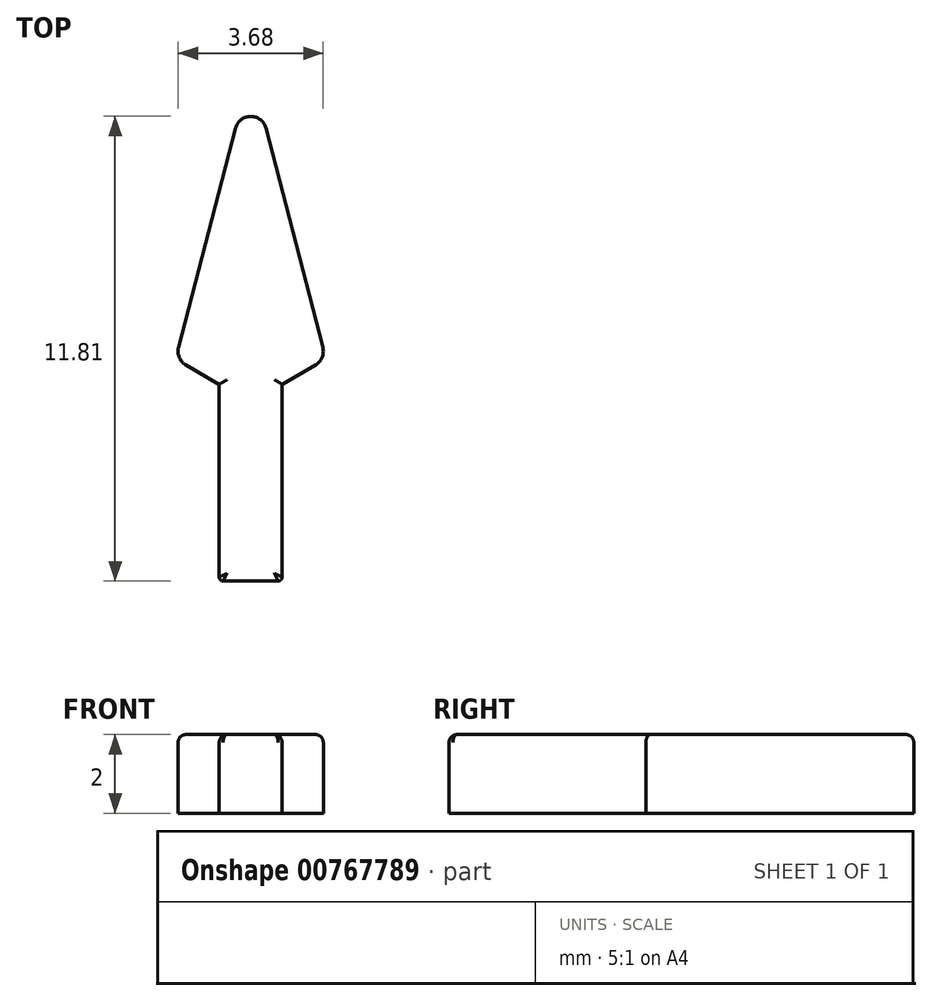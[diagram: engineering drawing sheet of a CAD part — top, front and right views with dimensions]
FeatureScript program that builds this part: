
annotation { "Feature Type Name" : "Feature", "Feature Type Description" : "" }
export const myFeature = defineFeature(function(context is Context, id is Id, definition is map)
    precondition{}
    {
        {
            var Q0;
            Q0=qCreatedBy(makeId("Top.planeOp"),FACE);
            var sketch = newSketch(context, id + "F0", { "sketchPlane" : qUnion([Q0])});
            skLineSegment(sketch, "E0.bottom", {"start": v(0, 0) * mm, "end": v(0.8, 0) * mm});
            skLineSegment(sketch, "E0.left", {"start": v(0, 0) * mm, "end": v(0, 5) * mm});
            skLineSegment(sketch, "E0.right", {"start": v(0.8, 0) * mm, "end": v(0.8, 5) * mm});
            skLineSegment(sketch, "E1", {"start": v(0.8, 5) * mm, "end": v(1.9, 5.64) * mm});
            skLineSegment(sketch, "E2", {"start": v(0, 5) * mm, "end": v(0, 13) * mm});
            skLineSegment(sketch, "E3", {"start": v(0, 13) * mm, "end": v(1.9, 5.64) * mm});
            skLineSegment(sketch, "E4.MirrorCS", {"start": v(0, 13) * mm, "end": v(-1.9, 5.64) * mm});
            skLineSegment(sketch, "E5.MirrorCS", {"start": v(-0.8, 5) * mm, "end": v(-1.9, 5.64) * mm});
            skLineSegment(sketch, "E6.MirrorCS", {"start": v(-0.8, 0) * mm, "end": v(-0.8, 5) * mm});
            skLineSegment(sketch, "E7.MirrorCS", {"start": v(0, 0) * mm, "end": v(-0.8, 0) * mm});
            skSolve(sketch);
        }
        {
            var Q0;
            Q0 = qSketchRegion(id + "F0", true);
            extrude(context, id + "F1", {"entities" : qUnion([Q0]), "depth" : 2 * mm, "offsetDistance" : 25 * mm});
        }
        {
            var Q0;
            Q0=makeQuery(id+"F1.opExtrude","CAP_FACE",FACE,{"disambiguationData":[OSD([sQuery(id+"F0.wireOp",EDGE,"E0.bottom"),sQuery(id+"F0.wireOp",EDGE,"E0.right"),sQuery(id+"F0.wireOp",EDGE,"E1"),sQuery(id+"F0.wireOp",EDGE,"E3"),sQuery(id+"F0.wireOp",EDGE,"E4.MirrorCS"),sQuery(id+"F0.wireOp",EDGE,"E5.MirrorCS"),sQuery(id+"F0.wireOp",EDGE,"E6.MirrorCS"),sQuery(id+"F0.wireOp",EDGE,"E7.MirrorCS")])],"isStart":false});
            fillet(context, id + "F2", {"entities" : qUnion([Q0]), "radius" : 0.2 * mm, "tangentPropagation" : true, "allowEdgeOverflow" : false});
        }
        {
            var Q0;
            Q0=makeQuery(id+"F1.opExtrude","SWEPT_EDGE",EDGE,{"disambiguationData":[OSD([sQuery(id+"F0.wireOp",EDGE,"E1"),sQuery(id+"F0.wireOp",EDGE,"E3")])]});
            var Q1;
            Q1=makeQuery(id+"F1.opExtrude","SWEPT_EDGE",EDGE,{"disambiguationData":[OSD([sQuery(id+"F0.wireOp",EDGE,"E4.MirrorCS"),sQuery(id+"F0.wireOp",EDGE,"E5.MirrorCS")])]});
            var Q2;
            Q2=makeQuery(id+"F1.opExtrude","SWEPT_EDGE",EDGE,{"disambiguationData":[OSD([sQuery(id+"F0.wireOp",EDGE,"E2"),sQuery(id+"F0.wireOp",EDGE,"E3"),sQuery(id+"F0.wireOp",EDGE,"E4.MirrorCS")])]});
            fillet(context, id + "F3", {"entities" : qUnion([Q0, Q1, Q2]), "radius" : 0.4 * mm, "tangentPropagation" : true, "allowEdgeOverflow" : false});
        }
        {
            var Q0;
            Q0=makeQuery(id+"F1.opExtrude","SWEPT_EDGE",EDGE,{"disambiguationData":[OSD([sQuery(id+"F0.wireOp",EDGE,"E0.bottom"),sQuery(id+"F0.wireOp",EDGE,"E0.right")])]});
            var Q1;
            Q1=makeQuery(id+"F1.opExtrude","SWEPT_EDGE",EDGE,{"disambiguationData":[OSD([sQuery(id+"F0.wireOp",EDGE,"E6.MirrorCS"),sQuery(id+"F0.wireOp",EDGE,"E7.MirrorCS")])]});
            fillet(context, id + "F4", {"entities" : qUnion([Q0, Q1]), "radius" : 0.1 * mm, "tangentPropagation" : true, "allowEdgeOverflow" : false});
        }
    });
